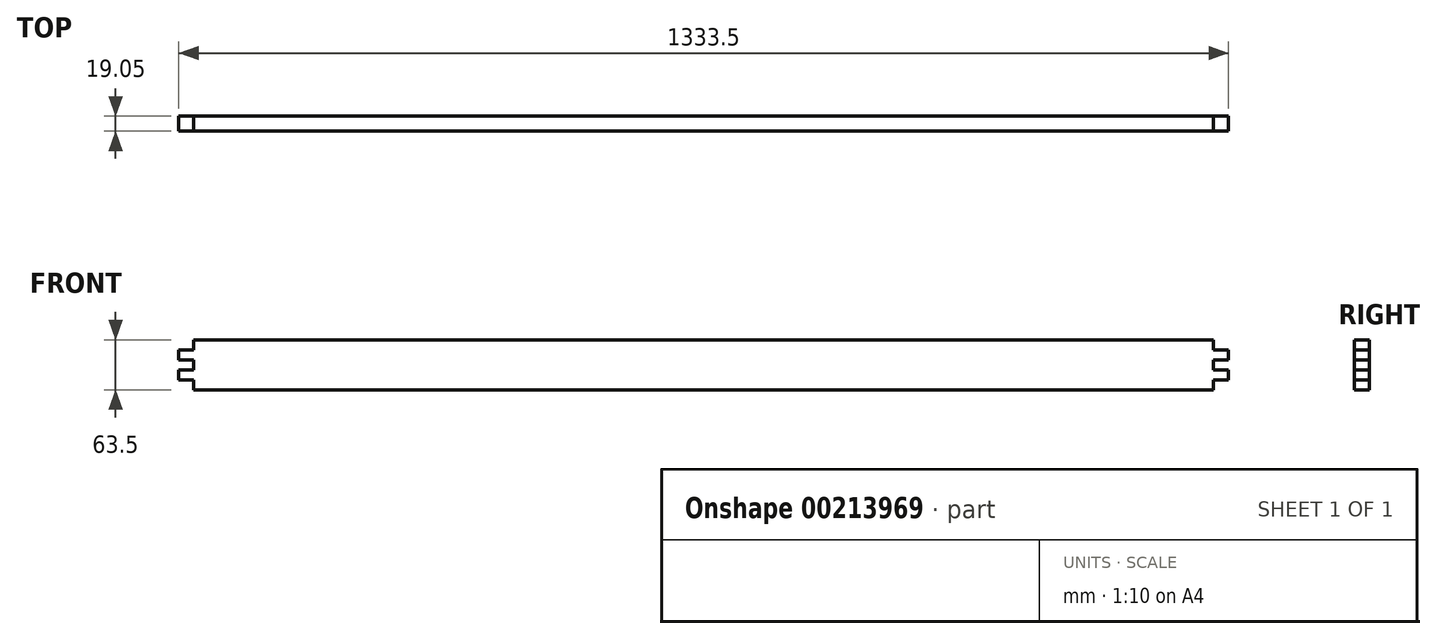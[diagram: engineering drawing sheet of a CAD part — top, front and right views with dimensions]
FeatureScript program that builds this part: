
annotation { "Feature Type Name" : "Feature", "Feature Type Description" : "" }
export const myFeature = defineFeature(function(context is Context, id is Id, definition is map)
    precondition{}
    {
        {
            var Q0;
            Q0=qCreatedBy(makeId("Front.planeOp"),FACE);
            var sketch = newSketch(context, id + "F0", { "sketchPlane" : qUnion([Q0])});
            skLineSegment(sketch, "E0", {"start": v(-647.7, 0) * mm, "end": v(647.7, 0) * mm});
            skLineSegment(sketch, "E1", {"start": v(647.7, 0) * mm, "end": v(647.7, 12.7) * mm});
            skLineSegment(sketch, "E2", {"start": v(647.7, 12.7) * mm, "end": v(666.75, 12.7) * mm});
            skLineSegment(sketch, "E3", {"start": v(666.75, 12.7) * mm, "end": v(666.75, 25.4) * mm});
            skLineSegment(sketch, "E4", {"start": v(666.75, 25.4) * mm, "end": v(647.7, 25.4) * mm});
            skLineSegment(sketch, "E5", {"start": v(647.7, 25.4) * mm, "end": v(647.7, 38.1) * mm});
            skLineSegment(sketch, "E6", {"start": v(647.7, 38.1) * mm, "end": v(666.75, 38.1) * mm});
            skLineSegment(sketch, "E7", {"start": v(666.75, 38.1) * mm, "end": v(666.75, 50.8) * mm});
            skLineSegment(sketch, "E8", {"start": v(666.75, 50.8) * mm, "end": v(647.7, 50.8) * mm});
            skLineSegment(sketch, "E9", {"start": v(647.7, 50.8) * mm, "end": v(647.7, 63.5) * mm});
            skLineSegment(sketch, "E10", {"start": v(647.7, 63.5) * mm, "end": v(-647.7, 63.5) * mm});
            skLineSegment(sketch, "E11", {"start": v(-647.7, 63.5) * mm, "end": v(-647.7, 50.8) * mm});
            skLineSegment(sketch, "E12", {"start": v(-647.7, 50.8) * mm, "end": v(-666.75, 50.8) * mm});
            skLineSegment(sketch, "E13", {"start": v(-666.75, 50.8) * mm, "end": v(-666.75, 38.1) * mm});
            skLineSegment(sketch, "E14", {"start": v(-666.75, 38.1) * mm, "end": v(-647.7, 38.1) * mm});
            skLineSegment(sketch, "E15", {"start": v(-647.7, 38.1) * mm, "end": v(-647.7, 25.4) * mm});
            skLineSegment(sketch, "E16", {"start": v(-647.7, 25.4) * mm, "end": v(-666.75, 25.4) * mm});
            skLineSegment(sketch, "E17", {"start": v(-666.75, 25.4) * mm, "end": v(-666.75, 12.7) * mm});
            skLineSegment(sketch, "E18", {"start": v(-666.75, 12.7) * mm, "end": v(-647.7, 12.7) * mm});
            skLineSegment(sketch, "E19", {"start": v(-647.7, 12.7) * mm, "end": v(-647.7, 0) * mm});
            skSolve(sketch);
        }
        {
            var Q0;
            Q0=makeQuery(id+"F0.imprint","IMPRINT",FACE,{"disambiguationData":[TD([[makeQuery(id+"F0.imprint","IMPRINT",EDGE,{"derivedFrom":sQuery(id+"F0.wireOp",EDGE,"E0")}),1.0]])]});
            extrude(context, id + "F1", {"entities" : qUnion([Q0]), "depth" : 19.05 * mm});
        }
    });
